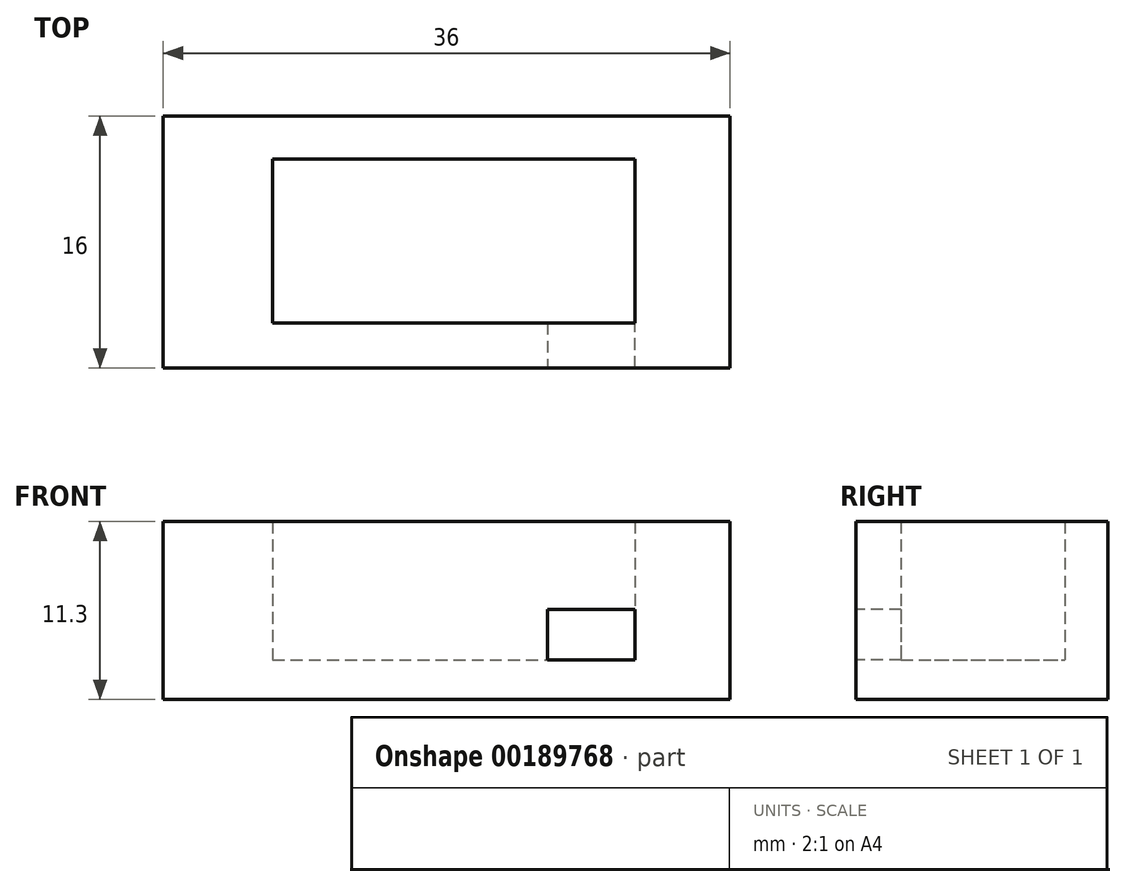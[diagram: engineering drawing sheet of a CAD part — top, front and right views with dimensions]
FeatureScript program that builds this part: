
annotation { "Feature Type Name" : "Feature", "Feature Type Description" : "" }
export const myFeature = defineFeature(function(context is Context, id is Id, definition is map)
    precondition{}
    {
        {
            var Q0;
            Q0=qCreatedBy(makeId("Top.planeOp"),FACE);
            var sketch = newSketch(context, id + "F0", { "sketchPlane" : qUnion([Q0])});
            skLineSegment(sketch, "E0.bottom", {"start": v(-15.72, 7.87) * mm, "end": v(20.28, 7.87) * mm});
            skLineSegment(sketch, "E0.top", {"start": v(-15.72, 23.87) * mm, "end": v(20.28, 23.87) * mm});
            skLineSegment(sketch, "E0.left", {"start": v(-15.72, 7.87) * mm, "end": v(-15.72, 23.87) * mm});
            skLineSegment(sketch, "E0.right", {"start": v(20.28, 7.87) * mm, "end": v(20.28, 23.87) * mm});
            skSolve(sketch);
        }
        {
            var Q0;
            Q0=makeQuery(id+"F0.imprint","IMPRINT",FACE,{"disambiguationData":[TD([[makeQuery(id+"F0.imprint","IMPRINT",EDGE,{"derivedFrom":sQuery(id+"F0.wireOp",EDGE,"E0.bottom")}),1.0]])]});
            extrude(context, id + "F1", {"entities" : qUnion([Q0]), "depth" : 2.5 * mm});
        }
        {
            var Q0;
            Q0=makeQuery(id+"F1.opExtrude","CAP_FACE",FACE,{"disambiguationData":[OSD([sQuery(id+"F0.wireOp",EDGE,"E0.bottom"),sQuery(id+"F0.wireOp",EDGE,"E0.top"),sQuery(id+"F0.wireOp",EDGE,"E0.left"),sQuery(id+"F0.wireOp",EDGE,"E0.right")])],"isStart":false});
            var sketch = newSketch(context, id + "F2", { "sketchPlane" : qUnion([Q0])});
            skLineSegment(sketch, "E1.bottom", {"start": v(-8.76, 10.74) * mm, "end": v(14.24, 10.74) * mm});
            skLineSegment(sketch, "E1.top", {"start": v(-8.76, 21.14) * mm, "end": v(14.24, 21.14) * mm});
            skLineSegment(sketch, "E1.left", {"start": v(-8.76, 10.74) * mm, "end": v(-8.76, 21.14) * mm});
            skLineSegment(sketch, "E1.right", {"start": v(14.24, 10.74) * mm, "end": v(14.24, 21.14) * mm});
            skLineSegment(sketch, "E2", {"start": v(-15.72, 23.87) * mm, "end": v(-22.02, 23.87) * mm, "construction": true});
            skLineSegment(sketch, "E3", {"start": v(-22.02, 23.87) * mm, "end": v(-22.02, 7.87) * mm, "construction": true});
            skLineSegment(sketch, "E4", {"start": v(-15.72, 7.87) * mm, "end": v(-22.02, 7.87) * mm, "construction": true});
            skLineSegment(sketch, "E5", {"start": v(-22.02, 15.87) * mm, "end": v(31.65, 15.87) * mm, "construction": true});
            skPoint(sketch, "E5.endSnap0", {"position": v(20.28, 15.87) * mm});
            skSolve(sketch);
        }
        {
            var Q0;
            Q0=makeQuery(id+"F2.imprint","IMPRINT",FACE,{"disambiguationData":[TD([[makeQuery(id+"F2.imprint","IMPRINT",EDGE,{"derivedFrom":sQuery(id+"F2.wireOp",EDGE,"E1.bottom")}),-1.0]])]});
            extrude(context, id + "F3", {"entities" : qUnion([Q0]), "operationType" : NewBodyOperationType.ADD, "depth" : 8.8 * mm});
        }
        {
            var Q0;
            {var subQ0=sQuery(id+"F0.wireOp",EDGE,"E0.bottom");Q0=makeQuery(id+"F3.boolean.opBoolean","MERGE",FACE,{"derivedFrom":[makeQuery(id+"F1.opExtrude","SWEPT_FACE",FACE,{"disambiguationData":[OSD([subQ0])]}),makeQuery(id+"F3.opExtrude","SWEPT_FACE",FACE,{"disambiguationData":[OSD([subQ0])]})]});}
            var sketch = newSketch(context, id + "F4", { "sketchPlane" : qUnion([Q0])});
            skCircle(sketch, "E6", {"center": v(-15.72, 0) * mm, "radius": 2.5 * mm, "construction": true});
            skLineSegment(sketch, "E7", {"start": v(-15.72, 2.5) * mm, "end": v(20.28, 2.5) * mm, "construction": true});
            skLineSegment(sketch, "E8", {"start": v(14.24, 14.1) * mm, "end": v(14.24, 0) * mm, "construction": true});
            skLineSegment(sketch, "E9.bottom", {"start": v(14.24, 2.5) * mm, "end": v(8.7, 2.5) * mm});
            skLineSegment(sketch, "E9.top", {"start": v(14.24, 5.73) * mm, "end": v(8.7, 5.73) * mm});
            skLineSegment(sketch, "E9.left", {"start": v(14.24, 2.5) * mm, "end": v(14.24, 5.73) * mm});
            skLineSegment(sketch, "E9.right", {"start": v(8.7, 2.5) * mm, "end": v(8.7, 5.73) * mm});
            skSolve(sketch);
        }
        {
            var Q0;
            Q0=makeQuery(id+"F4.imprint","IMPRINT",FACE,{"disambiguationData":[TD([[makeQuery(id+"F4.imprint","IMPRINT",EDGE,{"derivedFrom":sQuery(id+"F4.wireOp",EDGE,"E9.bottom")}),-1.0]])]});
            extrude(context, id + "F5", {"entities" : qUnion([Q0]), "operationType" : NewBodyOperationType.REMOVE, "oppositeDirection" : true, "depth" : 5 * mm});
        }
    });
